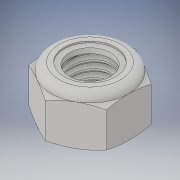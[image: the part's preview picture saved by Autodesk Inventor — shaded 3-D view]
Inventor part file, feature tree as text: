
AUTODESK INVENTOR PART (.ipt)
format: ipt  version: 2018 (Build 220112000, 112)  size: 297,984 bytes
history: native  units: in
note: dims shown in document units (in); Inventor stores cm internally (conversion verified against a paired STEP export)
features: other x1, revolve x1
ambient origin geometry x8: Origin, YZ Plane, XZ Plane, XY Plane, X Axis, Y Axis, Z Axis, Center Point
bodies: Solid1 (feature_tree), Solid2 (feature_tree)
feature tree (2):
  other  "Cut-Revolve4"
  revolve  "Revolve2"  [1 undecoded]
note: 1 required parameter value undecoded (feature->parameter linkage not recoverable at this tier; creation-order binding heuristic only, values carry confidence <= 0.55)
